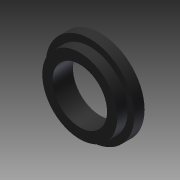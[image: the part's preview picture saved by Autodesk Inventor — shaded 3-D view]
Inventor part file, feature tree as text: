
AUTODESK INVENTOR PART (.ipt)
format: ipt  version: 2012 (Build 160160000, 160)  size: 90,112 bytes
history: native  units: in
note: dims shown in document units (in); Inventor stores cm internally (conversion verified against a paired STEP export)
features: extrude x2, sketch x1
ambient origin geometry x8: Origin, YZ Plane, XZ Plane, XY Plane, X Axis, Y Axis, Z Axis, Center Point
bodies: Solid1 (feature_tree)
feature tree (3):
  sketch  "Sketch1"  dims[d0=1.0in d1=1.375in d2=1.625in d3=0.375in d4=0.0in d5=0.1875in d6=0.0in]
  extrude  "Extrusion1"  Depth=1.375in
  extrude  "Extrusion2"  Depth=1.625in
